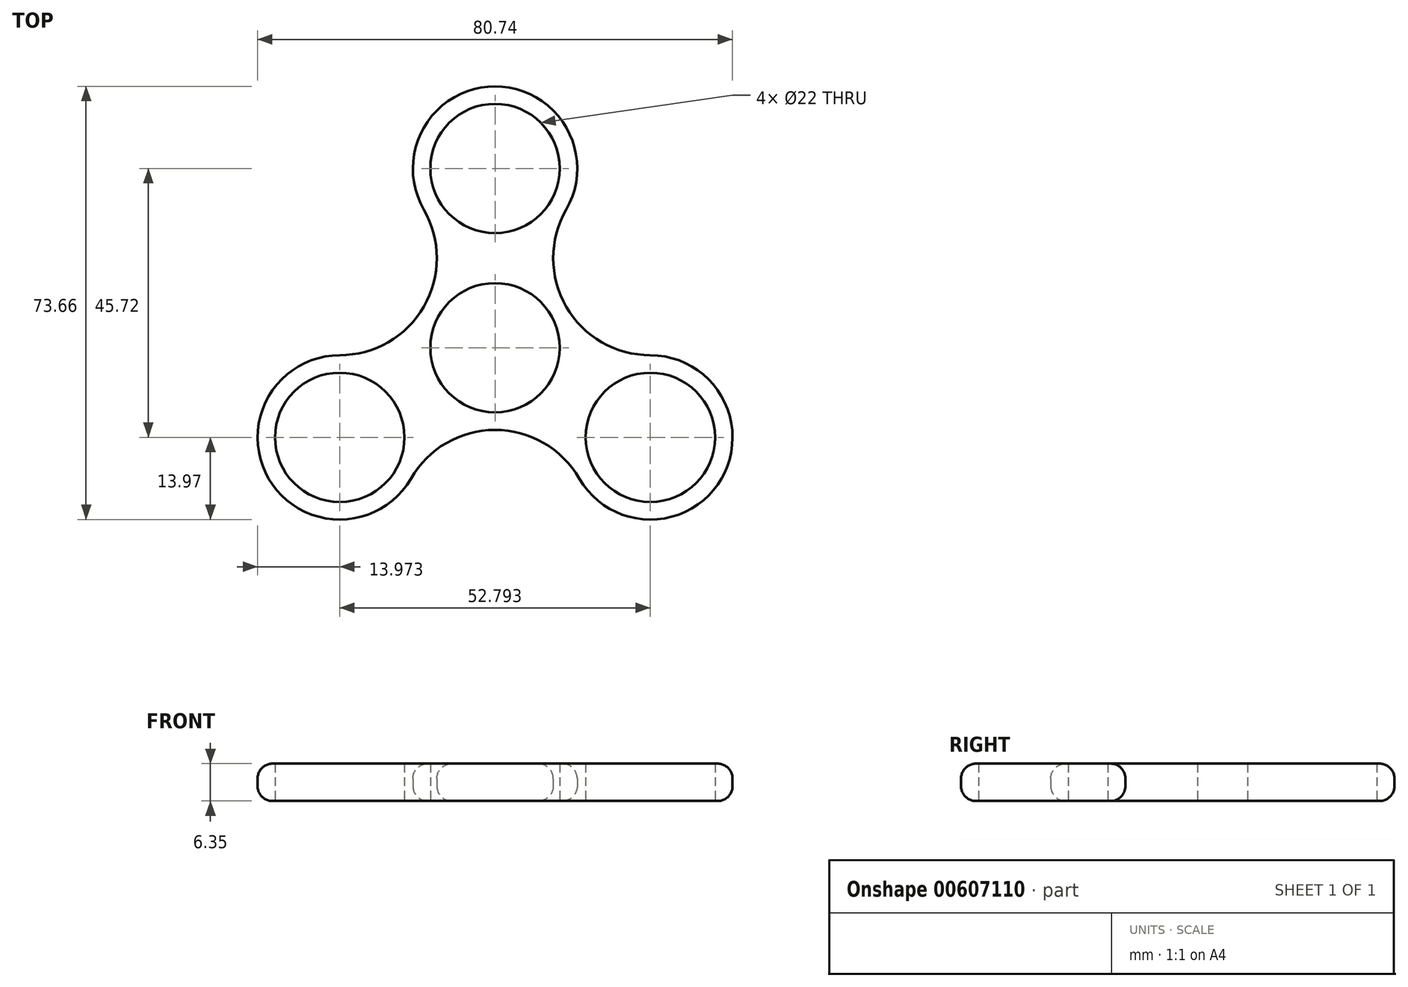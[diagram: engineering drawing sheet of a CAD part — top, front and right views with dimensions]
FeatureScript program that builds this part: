
annotation { "Feature Type Name" : "Feature", "Feature Type Description" : "" }
export const myFeature = defineFeature(function(context is Context, id is Id, definition is map)
    precondition{}
    {
        {
            var Q0;
            Q0=qCreatedBy(makeId("Top.planeOp"),FACE);
            var sketch = newSketch(context, id + "F0", { "sketchPlane" : qUnion([Q0])});
            skCircle(sketch, "E0", {"center": v(0, 30.48) * mm, "radius": 13.97 * mm});
            skCircle(sketch, "E1.1.0", {"center": v(-26.4, -15.24) * mm, "radius": 13.97 * mm});
            skCircle(sketch, "E1.2.0", {"center": v(26.4, -15.24) * mm, "radius": 13.97 * mm});
            skPoint(sketch, "E1.center", {"position": v(0, 0) * mm});
            skCircle(sketch, "E2", {"center": v(0, 0) * mm, "radius": 11 * mm});
            skSolve(sketch);
        }
        {
            var Q0;
            Q0=qCreatedBy(makeId("Top.planeOp"),FACE);
            var sketch = newSketch(context, id + "F1", { "sketchPlane" : qUnion([Q0])});
            skCircle(sketch, "E3", {"center": v(0, 30.48) * mm, "radius": 11 * mm});
            skCircle(sketch, "E4.1.0", {"center": v(-26.4, -15.24) * mm, "radius": 11 * mm});
            skCircle(sketch, "E4.2.0", {"center": v(26.4, -15.24) * mm, "radius": 11 * mm});
            skPoint(sketch, "E4.center", {"position": v(0, 0) * mm});
            skArc(sketch, "E5.0", {"start": v(12.1, 23.5) * mm, "mid": v(0, 44.45) * mm, "end": v(-12.1, 23.5) * mm});
            skArc(sketch, "E6.0", {"start": v(14.3, -22.23) * mm, "mid": v(38.5, -22.22) * mm, "end": v(26.4, -1.27) * mm});
            skCircle(sketch, "E7.0", {"center": v(0, 0) * mm, "radius": 11 * mm});
            skArc(sketch, "E8.0", {"start": v(-26.4, -1.27) * mm, "mid": v(-38.5, -22.23) * mm, "end": v(-14.3, -22.23) * mm});
            skArc(sketch, "E9", {"start": v(12.1, 23.5) * mm, "mid": v(12.1, 6.99) * mm, "end": v(26.4, -1.27) * mm});
            skArc(sketch, "E10.1.0", {"start": v(-26.4, -1.27) * mm, "mid": v(-12.1, 6.99) * mm, "end": v(-12.1, 23.5) * mm});
            skArc(sketch, "E10.2.0", {"start": v(14.3, -22.23) * mm, "mid": v(0, -13.97) * mm, "end": v(-14.3, -22.22) * mm});
            skSolve(sketch);
        }
        {
            var Q0;
            Q0=makeQuery(id+"F1.imprint","IMPRINT",FACE,{"disambiguationData":[TD([[makeQuery(id+"F1.imprint","IMPRINT",EDGE,{"derivedFrom":sQuery(id+"F1.wireOp",EDGE,"E3")}),-1.0]])]});
            extrude(context, id + "F2", {"entities" : qUnion([Q0]), "depth" : 6.35 * mm, "offsetDistance" : 25.4 * mm});
        }
        {
            var Q0;
            Q0=makeQuery(id+"F2.opExtrude","CAP_EDGE",EDGE,{"disambiguationData":[OSD([sQuery(id+"F1.wireOp",EDGE,"E10.2.0")])],"isStart":false});
            var Q1;
            Q1=makeQuery(id+"F2.opExtrude","CAP_EDGE",EDGE,{"disambiguationData":[OSD([sQuery(id+"F1.wireOp",EDGE,"E10.2.0")])],"isStart":true});
            fillet(context, id + "F3", {"entities" : qUnion([Q0, Q1]), "radius" : 2.54 * mm, "tangentPropagation" : true, "allowEdgeOverflow" : false});
        }
    });
